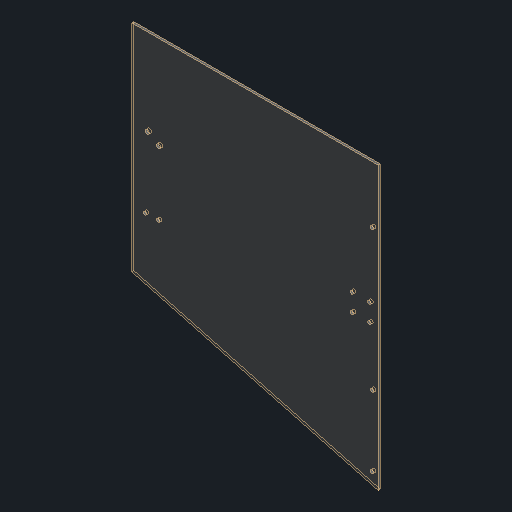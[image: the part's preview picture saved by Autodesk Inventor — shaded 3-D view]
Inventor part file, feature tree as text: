
AUTODESK INVENTOR PART (.ipt)
format: ipt  version: 2024.3 (Build 283343010, 343A)  size: 77,824 bytes
history: native  units: mm (DEFAULTED — no unit token found)
features: other x3, sketch x1
ambient origin geometry x8: Origin, YZ Plane, XZ Plane, XY Plane, X Axis, Y Axis, Z Axis, Center Point
bodies: Solid1 (feature_tree)
feature tree (4):
  other  "hopper_side_l.ipt"
  other  "Solid1::hopper_side_l.ipt"
  other  "TaggingFeature1"
  sketch  "Sketch1"  dims[d0=10.0mm d1=3.048mm]
